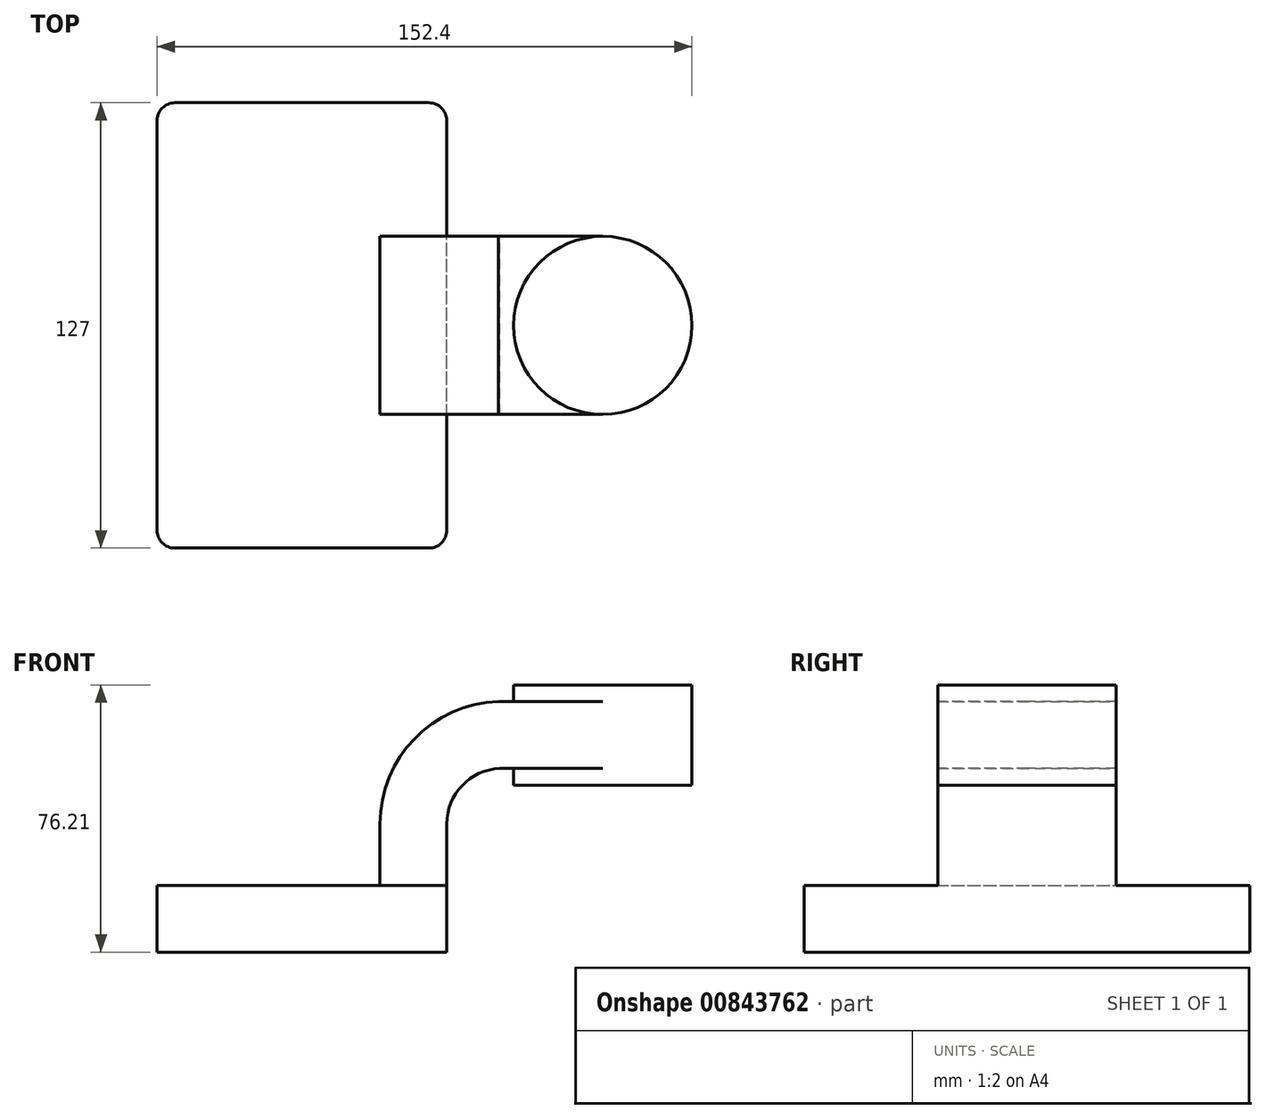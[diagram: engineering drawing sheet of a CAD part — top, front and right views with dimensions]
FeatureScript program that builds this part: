
annotation { "Feature Type Name" : "Feature", "Feature Type Description" : "" }
export const myFeature = defineFeature(function(context is Context, id is Id, definition is map)
    precondition{}
    {
        {
            var Q0;
            Q0=qCreatedBy(makeId("Front.planeOp"),FACE);
            var sketch = newSketch(context, id + "F0", { "sketchPlane" : qUnion([Q0])});
            skLineSegment(sketch, "E0.bottom", {"start": v(-41.28, -9.53) * mm, "end": v(41.28, -9.53) * mm});
            skLineSegment(sketch, "E0.top", {"start": v(-41.28, 9.53) * mm, "end": v(41.28, 9.53) * mm});
            skLineSegment(sketch, "E0.left", {"start": v(-41.28, -9.53) * mm, "end": v(-41.28, 9.53) * mm});
            skLineSegment(sketch, "E0.right", {"start": v(41.28, -9.53) * mm, "end": v(41.28, 9.53) * mm});
            skPoint(sketch, "E0.middle", {"position": v(0, 0) * mm});
            skLineSegment(sketch, "E1.bottom", {"start": v(111.12, 38.1) * mm, "end": v(60.32, 38.1) * mm});
            skLineSegment(sketch, "E1.top", {"start": v(111.12, 66.68) * mm, "end": v(60.32, 66.68) * mm});
            skLineSegment(sketch, "E1.left", {"start": v(111.12, 38.1) * mm, "end": v(111.12, 66.68) * mm});
            skLineSegment(sketch, "E1.right", {"start": v(60.32, 38.1) * mm, "end": v(60.32, 66.68) * mm});
            skPoint(sketch, "E1.middle", {"position": v(85.72, 52.39) * mm});
            skLineSegment(sketch, "E2", {"start": v(41.28, 9.52) * mm, "end": v(41.28, 27.02) * mm});
            skArc(sketch, "E3", {"start": v(41.28, 27.02) * mm, "mid": v(45.65, 37.97) * mm, "end": v(56.37, 42.88) * mm});
            skLineSegment(sketch, "E4", {"start": v(56.37, 42.88) * mm, "end": v(85.72, 42.88) * mm});
            skLineSegment(sketch, "E5.0", {"start": v(56, 61.93) * mm, "end": v(85.72, 61.93) * mm});
            skArc(sketch, "E5.1", {"start": v(22.23, 27.02) * mm, "mid": v(32.05, 51.3) * mm, "end": v(56, 61.93) * mm});
            skLineSegment(sketch, "E5.2", {"start": v(22.22, 9.52) * mm, "end": v(22.22, 27.02) * mm});
            skLineSegment(sketch, "E6", {"start": v(85.72, 38.1) * mm, "end": v(85.72, 66.68) * mm});
            skFitSpline(sketch, "E7", {"points": [v(-41.28, 9.53) * mm, v(56, 61.93) * mm], "startDerivative": vector(-1.16, 62.25) * mm, "endDerivative": vector(105.42, 1.93) * mm});
            skSolve(sketch);
        }
        {
            var Q0;
            Q0=makeQuery(id+"F0.imprint","IMPRINT",FACE,{"disambiguationData":[TD([[makeQuery(id+"F0.imprint","IMPRINT",EDGE,{"derivedFrom":sQuery(id+"F0.wireOp",EDGE,"E0.bottom")}),1.0]])]});
            extrude(context, id + "F1", {"entities" : qUnion([Q0]), "endBound" : BoundingType.SYMMETRIC, "depth" : 127 * mm, "offsetDistance" : 25.4 * mm});
        }
        {
            var Q0;
            Q0=makeQuery(id+"F0.imprint","IMPRINT",FACE,{"disambiguationData":[TD([[makeQuery(id+"F0.imprint","IMPRINT",EDGE,{"derivedFrom":sQuery(id+"F0.wireOp",EDGE,"E5.1")}),1.0]])]});
            extrude(context, id + "F2", {"entities" : qUnion([Q0]), "operationType" : NewBodyOperationType.ADD, "endBound" : BoundingType.SYMMETRIC, "depth" : 15.88 * mm, "offsetDistance" : 25.4 * mm});
        }
        {
            var Q0;
            {var subQ1=sQuery(id+"F0.wireOp",EDGE,"E2");Q0=makeQuery(id+"F0.imprint","IMPRINT",FACE,{"disambiguationData":[TD([[makeQuery(id+"F0.imprint","IMPRINT",EDGE,{"derivedFrom":subQ1}),1.0]])]});}
            var Q1;
            {var subQ0=sQuery(id+"F0.wireOp",EDGE,"E4");var subQ1=sQuery(id+"F0.wireOp",EDGE,"E1.right");var subQ2=makeQuery(id+"F0.imprint","INTERSECT",VERTEX,{"derivedFrom":[subQ1,subQ0]});Q1=makeQuery(id+"F0.imprint","IMPRINT",FACE,{"disambiguationData":[TD([[makeQuery(id+"F0.imprint","IMPRINT",EDGE,{"disambiguationData":[TD([[subQ2,-1.0]])],"derivedFrom":subQ1}),-1.0]])]});}
            extrude(context, id + "F3", {"entities" : qUnion([Q0, Q1]), "operationType" : NewBodyOperationType.ADD, "endBound" : BoundingType.SYMMETRIC, "depth" : 50.8 * mm, "offsetDistance" : 25.4 * mm});
        }
        {
            var Q0;
            {var subQ4=sQuery(id+"F0.wireOp",EDGE,"E1.left");Q0=makeQuery(id+"F0.imprint","IMPRINT",FACE,{"disambiguationData":[TD([[makeQuery(id+"F0.imprint","IMPRINT",EDGE,{"derivedFrom":subQ4}),1.0]])]});}
            var Q1;
            Q1=sQuery(id+"F0.wireOp",EDGE,"E6");
            revolve(context, id + "F4", {"operationType" : NewBodyOperationType.ADD, "surfaceOperationType" : NewSurfaceOperationType.NEW, "entities" : qUnion([Q0]), "axis" : qUnion([Q1]), "revolveType" : RevolveType.FULL});
        }
        {
            var Q0;
            Q0=makeQuery(id+"F1.opExtrude","CAP_EDGE",EDGE,{"disambiguationData":[OSD([sQuery(id+"F0.wireOp",EDGE,"E0.right")])],"isStart":false});
            var Q1;
            Q1=makeQuery(id+"F1.opExtrude","CAP_EDGE",EDGE,{"disambiguationData":[OSD([sQuery(id+"F0.wireOp",EDGE,"E0.left")])],"isStart":false});
            var Q2;
            Q2=makeQuery(id+"F1.opExtrude","CAP_EDGE",EDGE,{"disambiguationData":[OSD([sQuery(id+"F0.wireOp",EDGE,"E0.right")])],"isStart":true});
            var Q3;
            Q3=makeQuery(id+"F1.opExtrude","CAP_EDGE",EDGE,{"disambiguationData":[OSD([sQuery(id+"F0.wireOp",EDGE,"E0.left")])],"isStart":true});
            fillet(context, id + "F5", {"entities" : qUnion([Q0, Q1, Q2, Q3]), "radius" : 5.08 * mm, "tangentPropagation" : true, "allowEdgeOverflow" : false});
        }
    });
